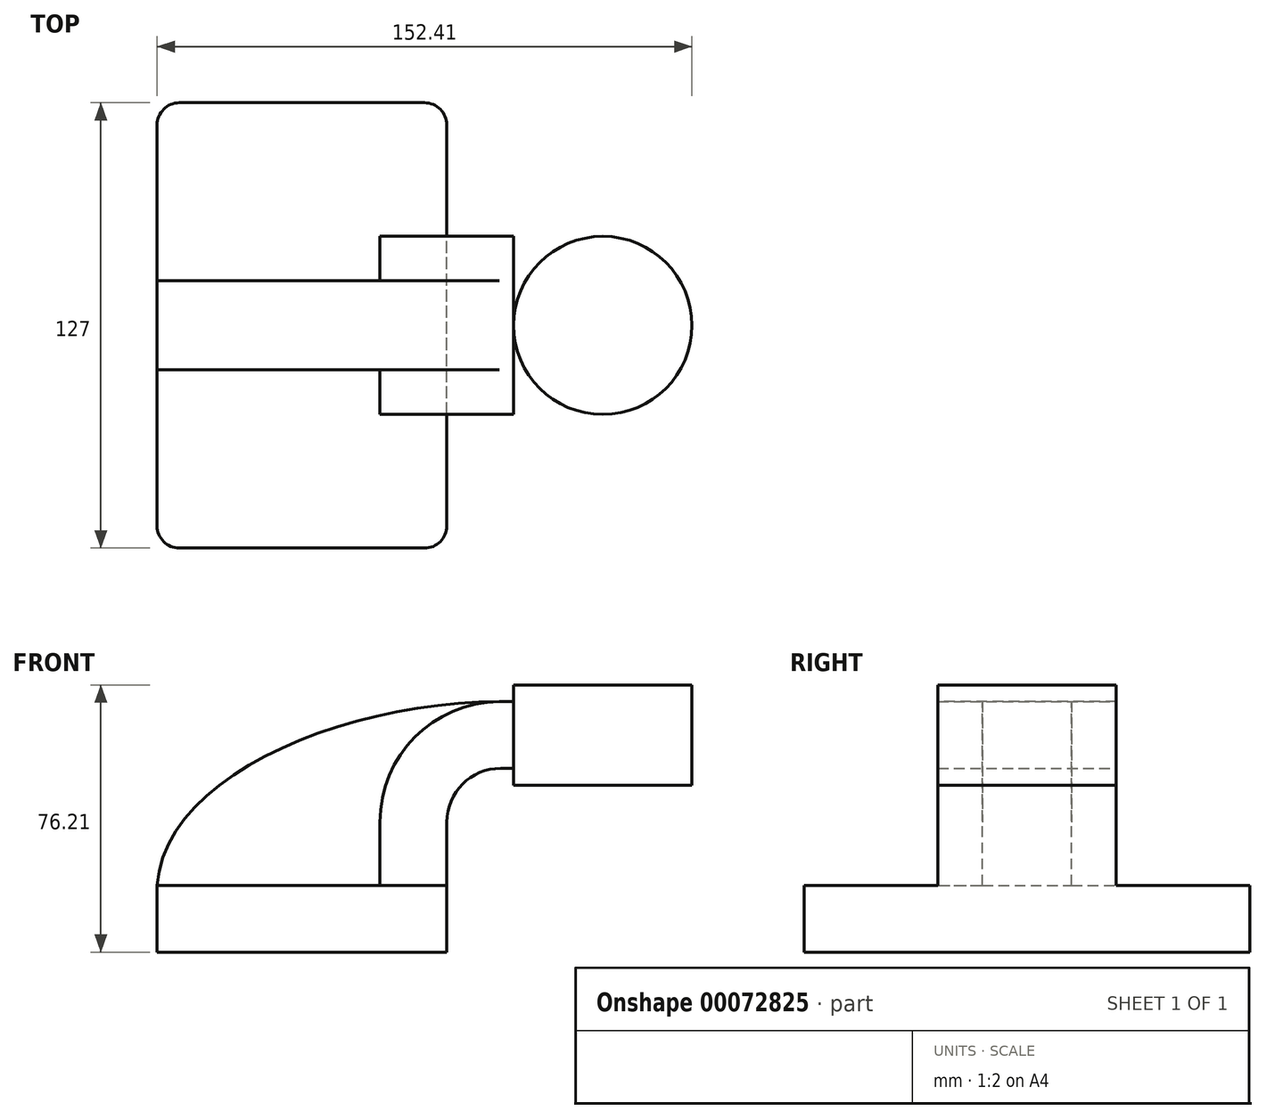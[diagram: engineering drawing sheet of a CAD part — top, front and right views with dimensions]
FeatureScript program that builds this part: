
annotation { "Feature Type Name" : "Feature", "Feature Type Description" : "" }
export const myFeature = defineFeature(function(context is Context, id is Id, definition is map)
    precondition{}
    {
        {
            var Q0;
            Q0=qCreatedBy(makeId("Front.planeOp"),FACE);
            var sketch = newSketch(context, id + "F0", { "sketchPlane" : qUnion([Q0])});
            skLineSegment(sketch, "E0.rect.bottom", {"start": v(-41.28, 9.52) * mm, "end": v(41.28, 9.52) * mm});
            skLineSegment(sketch, "E0.rect.top", {"start": v(-41.28, -9.52) * mm, "end": v(41.28, -9.52) * mm});
            skLineSegment(sketch, "E0.rect.left", {"start": v(-41.28, 9.52) * mm, "end": v(-41.28, -9.52) * mm});
            skLineSegment(sketch, "E0.rect.right", {"start": v(41.28, 9.52) * mm, "end": v(41.28, -9.52) * mm});
            skPoint(sketch, "E0.rect.middle", {"position": v(0, 0) * mm});
            skLineSegment(sketch, "E1.rect.bottom", {"start": v(111.12, 38.1) * mm, "end": v(60.32, 38.1) * mm});
            skLineSegment(sketch, "E1.rect.top", {"start": v(111.12, 66.68) * mm, "end": v(60.32, 66.68) * mm});
            skLineSegment(sketch, "E1.rect.left", {"start": v(111.12, 38.1) * mm, "end": v(111.12, 66.68) * mm});
            skLineSegment(sketch, "E1.rect.right", {"start": v(60.32, 38.1) * mm, "end": v(60.32, 66.68) * mm});
            skPoint(sketch, "E1.rect.middle", {"position": v(85.72, 52.39) * mm});
            skLineSegment(sketch, "E2", {"start": v(41.28, 9.52) * mm, "end": v(41.28, 27.55) * mm});
            skArc(sketch, "E3", {"start": v(41.27, 27.55) * mm, "mid": v(45.76, 38.39) * mm, "end": v(56.6, 42.88) * mm});
            skLineSegment(sketch, "E4", {"start": v(56.6, 42.88) * mm, "end": v(85.72, 42.88) * mm});
            skLineSegment(sketch, "E5.0", {"start": v(56.6, 61.93) * mm, "end": v(85.72, 61.93) * mm});
            skArc(sketch, "E5.1", {"start": v(22.22, 27.55) * mm, "mid": v(32.3, 51.86) * mm, "end": v(56.6, 61.93) * mm});
            skLineSegment(sketch, "E5.2", {"start": v(22.22, 9.52) * mm, "end": v(22.22, 27.55) * mm});
            skLineSegment(sketch, "E6", {"start": v(85.72, 38.1) * mm, "end": v(85.72, 66.68) * mm});
            skFitSpline(sketch, "E7", {"points": [v(-41.28, 9.53) * mm, v(56.6, 61.93) * mm], "startDerivative": vector(6.87, 95.2) * mm, "endDerivative": vector(132.58, 0.54) * mm});
            skSolve(sketch);
        }
        {
            var Q0;
            Q0=makeQuery(id+"F0.imprint","IMPRINT",FACE,{"disambiguationData":[TD([[makeQuery(id+"F0.imprint","IMPRINT",EDGE,{"derivedFrom":sQuery(id+"F0.wireOp",EDGE,"E0.rect.top")}),1.0]])]});
            extrude(context, id + "F1", {"entities" : qUnion([Q0]), "endBound" : BoundingType.SYMMETRIC, "depth" : 127 * mm});
        }
        {
            var Q0;
            {var subQ7=sQuery(id+"F0.wireOp",EDGE,"E2");Q0=makeQuery(id+"F0.imprint","IMPRINT",FACE,{"disambiguationData":[TD([[makeQuery(id+"F0.imprint","IMPRINT",EDGE,{"derivedFrom":subQ7}),1.0]])]});}
            extrude(context, id + "F2", {"entities" : qUnion([Q0]), "operationType" : NewBodyOperationType.ADD, "endBound" : BoundingType.SYMMETRIC, "depth" : 50.8 * mm});
        }
        {
            var Q0;
            {var subQ3=sQuery(id+"F0.wireOp",EDGE,"E5.2");Q0=makeQuery(id+"F0.imprint","IMPRINT",FACE,{"disambiguationData":[TD([[makeQuery(id+"F0.imprint","IMPRINT",EDGE,{"derivedFrom":subQ3}),1.0]])]});}
            extrude(context, id + "F3", {"entities" : qUnion([Q0]), "operationType" : NewBodyOperationType.ADD, "endBound" : BoundingType.SYMMETRIC, "depth" : 25.4 * mm});
        }
        {
            var Q0;
            {var subQ4=sQuery(id+"F0.wireOp",EDGE,"E1.rect.left");Q0=makeQuery(id+"F0.imprint","IMPRINT",FACE,{"disambiguationData":[TD([[makeQuery(id+"F0.imprint","IMPRINT",EDGE,{"derivedFrom":subQ4}),1.0]])]});}
            var Q1;
            Q1=sQuery(id+"F0.wireOp",EDGE,"E6");
            revolve(context, id + "F4", {"operationType" : NewBodyOperationType.ADD, "entities" : qUnion([Q0]), "axis" : qUnion([Q1]), "revolveType" : RevolveType.FULL});
        }
        {
            var Q0;
            Q0=makeQuery(id+"F1.opExtrude","CAP_EDGE",EDGE,{"disambiguationData":[OSD([sQuery(id+"F0.wireOp",EDGE,"E0.rect.right")])],"isStart":false});
            var Q1;
            Q1=makeQuery(id+"F1.opExtrude","CAP_EDGE",EDGE,{"disambiguationData":[OSD([sQuery(id+"F0.wireOp",EDGE,"E0.rect.left")])],"isStart":false});
            var Q2;
            Q2=makeQuery(id+"F1.opExtrude","CAP_EDGE",EDGE,{"disambiguationData":[OSD([sQuery(id+"F0.wireOp",EDGE,"E0.rect.right")])],"isStart":true});
            var Q3;
            Q3=makeQuery(id+"F1.opExtrude","CAP_EDGE",EDGE,{"disambiguationData":[OSD([sQuery(id+"F0.wireOp",EDGE,"E0.rect.left")])],"isStart":true});
            fillet(context, id + "F5", {"entities" : qUnion([Q0, Q1, Q2, Q3]), "radius" : 6.35 * mm, "tangentPropagation" : true, "allowEdgeOverflow" : false});
        }
    });
